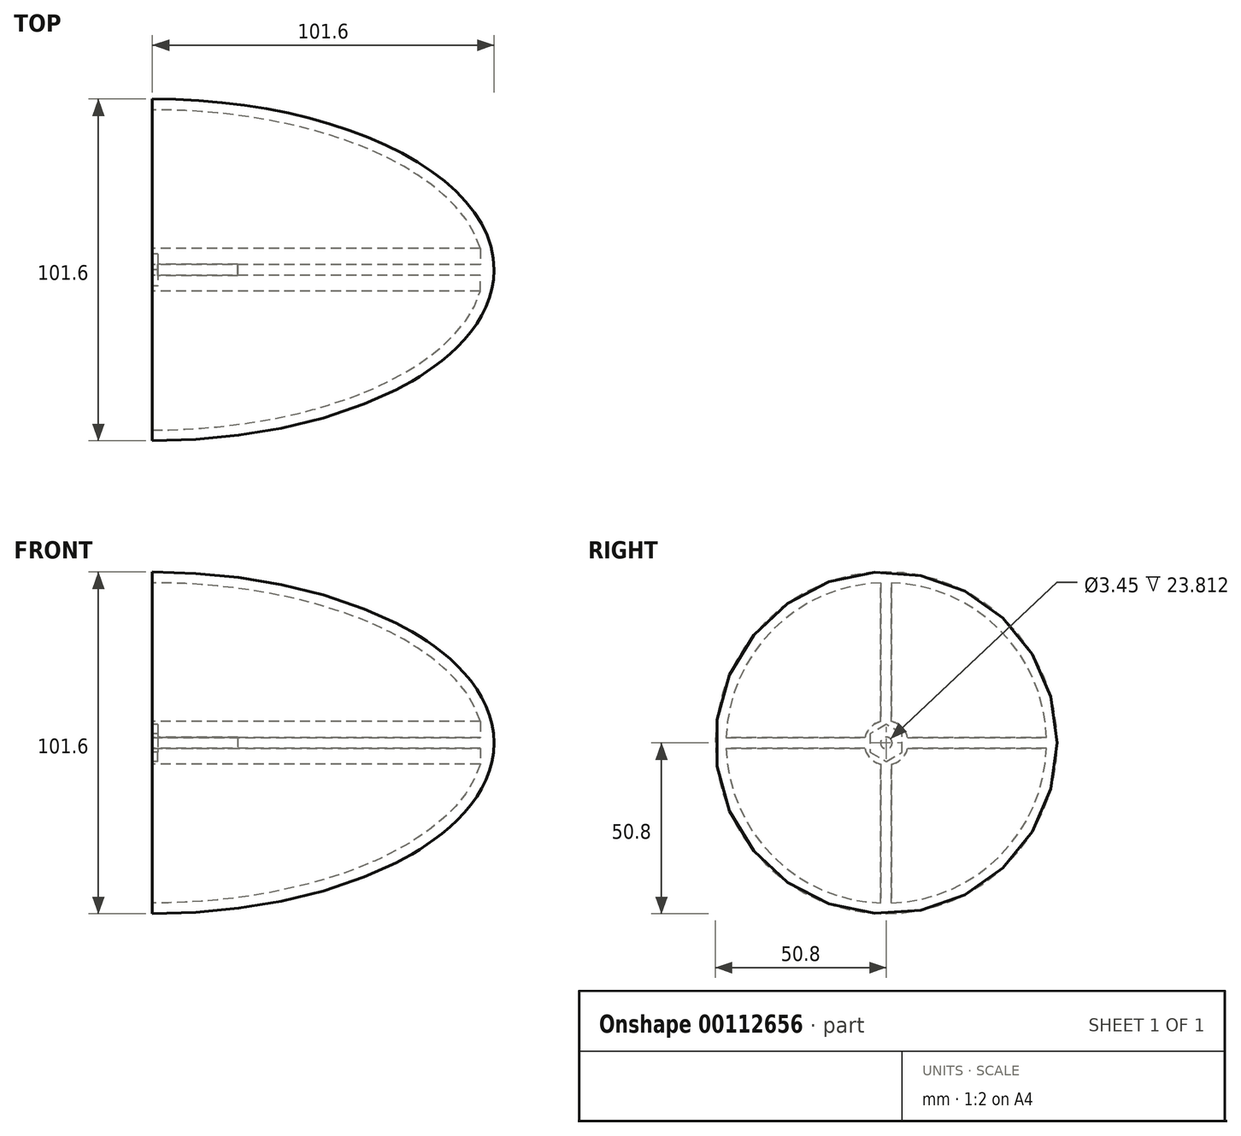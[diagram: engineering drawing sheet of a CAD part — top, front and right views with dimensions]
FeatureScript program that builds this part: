
annotation { "Feature Type Name" : "Feature", "Feature Type Description" : "" }
export const myFeature = defineFeature(function(context is Context, id is Id, definition is map)
    precondition{}
    {
        {
            var Q0;
            Q0=qCreatedBy(makeId("Top.planeOp"),FACE);
            var sketch = newSketch(context, id + "F0", { "sketchPlane" : qUnion([Q0])});
            skEllipse(sketch, "E0", {"center": v(0, 0) * mm, "majorRadius": 101.6 * mm, "minorRadius": 50.8 * mm, "majorAxis": v(-1, 0)});
            skLineSegment(sketch, "E1", {"start": v(101.6, 0) * mm, "end": v(-101.6, 0) * mm});
            skSolve(sketch);
        }
        {
            var Q0;
            Q0=qCreatedBy(makeId("Right.planeOp"),FACE);
            var sketch = newSketch(context, id + "F1", { "sketchPlane" : qUnion([Q0])});
            skCircle(sketch, "E2", {"center": v(0, 0) * mm, "radius": 50.8 * mm});
            skSolve(sketch);
        }
        {
            var Q0;
            {var subQ0=sQuery(id+"F0.wireOp",EDGE,"E1");Q0=makeQuery(id+"F0.imprint","IMPRINT",FACE,{"disambiguationData":[TD([[makeQuery(id+"F0.imprint","IMPRINT",EDGE,{"derivedFrom":subQ0}),-1.0]])]});}
            var Q1;
            Q1=sQuery(id+"F1.wireOp",EDGE,"E2");
            revolve(context, id + "F2", {"entities" : qUnion([Q0]), "axis" : qUnion([Q1]), "revolveType" : RevolveType.FULL});
        }
        {
            var Q0;
            Q0 = qSketchRegion(id + "F1", true);
            var Q1;
            Q1=makeQuery(id+"F2.opRevolve","SWEPT_FACE",FACE,{"disambiguationData":[OSD([sQuery(id+"F0.wireOp",EDGE,"E0")])]});
            extrude(context, id + "F3", {"entities" : qUnion([Q0]), "operationType" : NewBodyOperationType.REMOVE, "endBound" : BoundingType.UP_TO_SURFACE, "oppositeDirection" : true, "endBoundEntityFace" : qUnion([Q1]), "depth" : 25.4 * mm});
        }
        {
            var Q0;
            Q0=makeQuery(id+"F3.boolean.opBoolean","COPY",FACE,{"derivedFrom":makeQuery(id+"F3.opExtrude","CAP_FACE",FACE,{"disambiguationData":[OSD([sQuery(id+"F1.wireOp",EDGE,"E2")])],"isStart":true})});
            shell(context, id + "F4", {"entities" : qUnion([Q0]), "thickness" : 3.17 * mm});
        }
        {
            var Q0;
            Q0=makeQuery(id+"F3.boolean.opBoolean","COPY",FACE,{"derivedFrom":makeQuery(id+"F3.opExtrude","CAP_FACE",FACE,{"disambiguationData":[OSD([sQuery(id+"F1.wireOp",EDGE,"E2")])],"isStart":true})});
            var sketch = newSketch(context, id + "F5", { "sketchPlane" : qUnion([Q0])});
            skLineSegment(sketch, "E3.bottom", {"start": v(-47.6, -1.59) * mm, "end": v(-6.35, -1.59) * mm});
            skLineSegment(sketch, "E3.top", {"start": v(-47.6, 1.59) * mm, "end": v(-6.35, 1.59) * mm});
            skLineSegment(sketch, "E3.left", {"start": v(-47.6, -1.59) * mm, "end": v(-47.6, 1.59) * mm, "construction": true});
            skLineSegment(sketch, "E3.right", {"start": v(-6.35, -1.59) * mm, "end": v(-6.35, 1.59) * mm, "construction": true});
            skLineSegment(sketch, "E4.bottom", {"start": v(1.59, 47.6) * mm, "end": v(-1.59, 47.6) * mm, "construction": true});
            skLineSegment(sketch, "E4.top", {"start": v(1.59, 6.35) * mm, "end": v(-1.59, 6.35) * mm, "construction": true});
            skLineSegment(sketch, "E4.left", {"start": v(1.59, 47.6) * mm, "end": v(1.59, 6.35) * mm});
            skLineSegment(sketch, "E4.right", {"start": v(-1.59, 47.6) * mm, "end": v(-1.59, 6.35) * mm});
            skLineSegment(sketch, "E5.bottom", {"start": v(1.59, -47.6) * mm, "end": v(-1.59, -47.6) * mm, "construction": true});
            skLineSegment(sketch, "E5.top", {"start": v(1.59, -6.35) * mm, "end": v(-1.59, -6.35) * mm, "construction": true});
            skLineSegment(sketch, "E5.left", {"start": v(1.59, -47.6) * mm, "end": v(1.59, -6.35) * mm});
            skLineSegment(sketch, "E5.right", {"start": v(-1.59, -47.6) * mm, "end": v(-1.59, -6.35) * mm});
            skLineSegment(sketch, "E6", {"start": v(0, -6.35) * mm, "end": v(0, 6.35) * mm, "construction": true});
            skLineSegment(sketch, "E7", {"start": v(-6.35, 0) * mm, "end": v(6.35, 0) * mm, "construction": true});
            skLineSegment(sketch, "E8.top", {"start": v(-6.35, 6.35) * mm, "end": v(-1.59, 6.35) * mm});
            skLineSegment(sketch, "E8.left", {"start": v(-6.35, 1.59) * mm, "end": v(-6.35, 6.35) * mm});
            skLineSegment(sketch, "E9.top", {"start": v(-6.35, -6.35) * mm, "end": v(-1.59, -6.35) * mm});
            skLineSegment(sketch, "E9.left", {"start": v(-6.35, -1.59) * mm, "end": v(-6.35, -6.35) * mm});
            skLineSegment(sketch, "E10.bottom", {"start": v(6.35, -1.59) * mm, "end": v(47.6, -1.59) * mm});
            skLineSegment(sketch, "E10.top", {"start": v(6.35, 1.59) * mm, "end": v(47.6, 1.59) * mm});
            skLineSegment(sketch, "E10.left", {"start": v(6.35, -1.59) * mm, "end": v(6.35, 1.59) * mm, "construction": true});
            skLineSegment(sketch, "E10.right", {"start": v(47.6, -1.59) * mm, "end": v(47.6, 1.59) * mm, "construction": true});
            skLineSegment(sketch, "E11.bottom", {"start": v(1.59, -6.35) * mm, "end": v(6.35, -6.35) * mm});
            skLineSegment(sketch, "E11.right", {"start": v(6.35, -6.35) * mm, "end": v(6.35, -1.59) * mm});
            skLineSegment(sketch, "E12.top", {"start": v(6.35, 6.35) * mm, "end": v(1.59, 6.35) * mm});
            skLineSegment(sketch, "E12.left", {"start": v(6.35, 1.59) * mm, "end": v(6.35, 6.35) * mm});
            skCircle(sketch, "E13", {"center": v(0, 0) * mm, "radius": 47.63 * mm});
            skSolve(sketch);
        }
        {
            var Q0;
            {var subQ1=sQuery(id+"F5.wireOp",EDGE,"E3.bottom");Q0=makeQuery(id+"F5.imprint","IMPRINT",FACE,{"disambiguationData":[TD([[makeQuery(id+"F5.imprint","IMPRINT",EDGE,{"derivedFrom":subQ1}),1.0]])]});}
            var Q1;
            Q1=makeQuery(id+"F4.opShell","OFFSET_FACE",FACE,{"disambiguationData":[OSD([sQuery(id+"F0.wireOp",EDGE,"E0")])]});
            extrude(context, id + "F6", {"entities" : qUnion([Q0]), "operationType" : NewBodyOperationType.ADD, "endBound" : BoundingType.UP_TO_SURFACE, "oppositeDirection" : true, "endBoundEntityFace" : qUnion([Q1]), "depth" : 25.4 * mm});
        }
        {
            var Q0;
            Q0=makeQuery(id+"F6.boolean.opBoolean","MERGE",FACE,{"derivedFrom":[makeQuery(id+"F3.boolean.opBoolean","COPY",FACE,{"derivedFrom":makeQuery(id+"F3.opExtrude","CAP_FACE",FACE,{"disambiguationData":[OSD([sQuery(id+"F1.wireOp",EDGE,"E2")])],"isStart":true})}),makeQuery(id+"F6.opExtrude","CAP_FACE",FACE,{"disambiguationData":[OSD([sQuery(id+"F5.wireOp",EDGE,"E3.bottom"),sQuery(id+"F5.wireOp",EDGE,"E3.top"),sQuery(id+"F5.wireOp",EDGE,"E4.left"),sQuery(id+"F5.wireOp",EDGE,"E4.right"),sQuery(id+"F5.wireOp",EDGE,"E5.left"),sQuery(id+"F5.wireOp",EDGE,"E5.right"),sQuery(id+"F5.wireOp",EDGE,"E8.top"),sQuery(id+"F5.wireOp",EDGE,"E8.left"),sQuery(id+"F5.wireOp",EDGE,"E9.top"),sQuery(id+"F5.wireOp",EDGE,"E9.left"),sQuery(id+"F5.wireOp",EDGE,"E10.bottom"),sQuery(id+"F5.wireOp",EDGE,"E10.top"),sQuery(id+"F5.wireOp",EDGE,"E11.bottom"),sQuery(id+"F5.wireOp",EDGE,"E11.right"),sQuery(id+"F5.wireOp",EDGE,"E12.top"),sQuery(id+"F5.wireOp",EDGE,"E12.left"),sQuery(id+"F5.wireOp",EDGE,"E13")])],"isStart":true})]});
            var sketch = newSketch(context, id + "F7", { "sketchPlane" : qUnion([Q0])});
            skCircle(sketch, "E14", {"center": v(0, 0) * mm, "radius": 1.73 * mm});
            skSolve(sketch);
        }
        {
            var Q0;
            Q0 = qSketchRegion(id + "F7", true);
            extrude(context, id + "F8", {"entities" : qUnion([Q0]), "operationType" : NewBodyOperationType.REMOVE, "oppositeDirection" : true, "depth" : 25.4 * mm});
        }
        {
            var Q0;
            Q0=makeQuery(id+"F6.boolean.opBoolean","MERGE",FACE,{"derivedFrom":[makeQuery(id+"F3.boolean.opBoolean","COPY",FACE,{"derivedFrom":makeQuery(id+"F3.opExtrude","CAP_FACE",FACE,{"disambiguationData":[OSD([sQuery(id+"F1.wireOp",EDGE,"E2")])],"isStart":true})}),makeQuery(id+"F6.opExtrude","CAP_FACE",FACE,{"disambiguationData":[OSD([sQuery(id+"F5.wireOp",EDGE,"E3.bottom"),sQuery(id+"F5.wireOp",EDGE,"E3.top"),sQuery(id+"F5.wireOp",EDGE,"E4.left"),sQuery(id+"F5.wireOp",EDGE,"E4.right"),sQuery(id+"F5.wireOp",EDGE,"E5.left"),sQuery(id+"F5.wireOp",EDGE,"E5.right"),sQuery(id+"F5.wireOp",EDGE,"E8.top"),sQuery(id+"F5.wireOp",EDGE,"E8.left"),sQuery(id+"F5.wireOp",EDGE,"E9.top"),sQuery(id+"F5.wireOp",EDGE,"E9.left"),sQuery(id+"F5.wireOp",EDGE,"E10.bottom"),sQuery(id+"F5.wireOp",EDGE,"E10.top"),sQuery(id+"F5.wireOp",EDGE,"E11.bottom"),sQuery(id+"F5.wireOp",EDGE,"E11.right"),sQuery(id+"F5.wireOp",EDGE,"E12.top"),sQuery(id+"F5.wireOp",EDGE,"E12.left"),sQuery(id+"F5.wireOp",EDGE,"E13")])],"isStart":true})]});
            var sketch = newSketch(context, id + "F9", { "sketchPlane" : qUnion([Q0])});
            skCircle(sketch, "E15.cCircle", {"center": v(0, 0) * mm, "radius": 4.76 * mm, "construction": true});
            skLineSegment(sketch, "E15.0", {"start": v(4.76, 2.75) * mm, "end": v(4.76, -2.75) * mm});
            skLineSegment(sketch, "E15.1", {"start": v(4.76, -2.75) * mm, "end": v(0, -5.5) * mm});
            skLineSegment(sketch, "E15.2", {"start": v(0, -5.5) * mm, "end": v(-4.76, -2.75) * mm});
            skLineSegment(sketch, "E15.3", {"start": v(-4.76, -2.75) * mm, "end": v(-4.76, 2.75) * mm});
            skLineSegment(sketch, "E15.4", {"start": v(-4.76, 2.75) * mm, "end": v(0, 5.5) * mm});
            skLineSegment(sketch, "E15.5", {"start": v(0, 5.5) * mm, "end": v(4.76, 2.75) * mm});
            skPoint(sketch, "E15.0.midPoint", {"position": v(4.76, 0) * mm});
            skSolve(sketch);
        }
        {
            var Q0;
            Q0 = qSketchRegion(id + "F9", true);
            extrude(context, id + "F10", {"entities" : qUnion([Q0]), "operationType" : NewBodyOperationType.REMOVE, "oppositeDirection" : true, "depth" : 1.59 * mm});
        }
        {
            var Q0;
            Q0=makeQuery(id+"F6.opExtrude","SWEPT_EDGE",EDGE,{"disambiguationData":[OSD([sQuery(id+"F5.wireOp",EDGE,"E12.top"),sQuery(id+"F5.wireOp",EDGE,"E12.left")])]});
            var Q1;
            Q1=makeQuery(id+"F6.opExtrude","SWEPT_EDGE",EDGE,{"disambiguationData":[OSD([sQuery(id+"F5.wireOp",EDGE,"E8.top"),sQuery(id+"F5.wireOp",EDGE,"E8.left")])]});
            var Q2;
            Q2=makeQuery(id+"F6.opExtrude","SWEPT_EDGE",EDGE,{"disambiguationData":[OSD([sQuery(id+"F5.wireOp",EDGE,"E9.top"),sQuery(id+"F5.wireOp",EDGE,"E9.left")])]});
            var Q3;
            Q3=makeQuery(id+"F6.opExtrude","SWEPT_EDGE",EDGE,{"disambiguationData":[OSD([sQuery(id+"F5.wireOp",EDGE,"E11.bottom"),sQuery(id+"F5.wireOp",EDGE,"E11.right")])]});
            fillet(context, id + "F11", {"entities" : qUnion([Q0, Q1, Q2, Q3]), "radius" : 6.35 * mm, "tangentPropagation" : true, "allowEdgeOverflow" : false});
        }
    });
